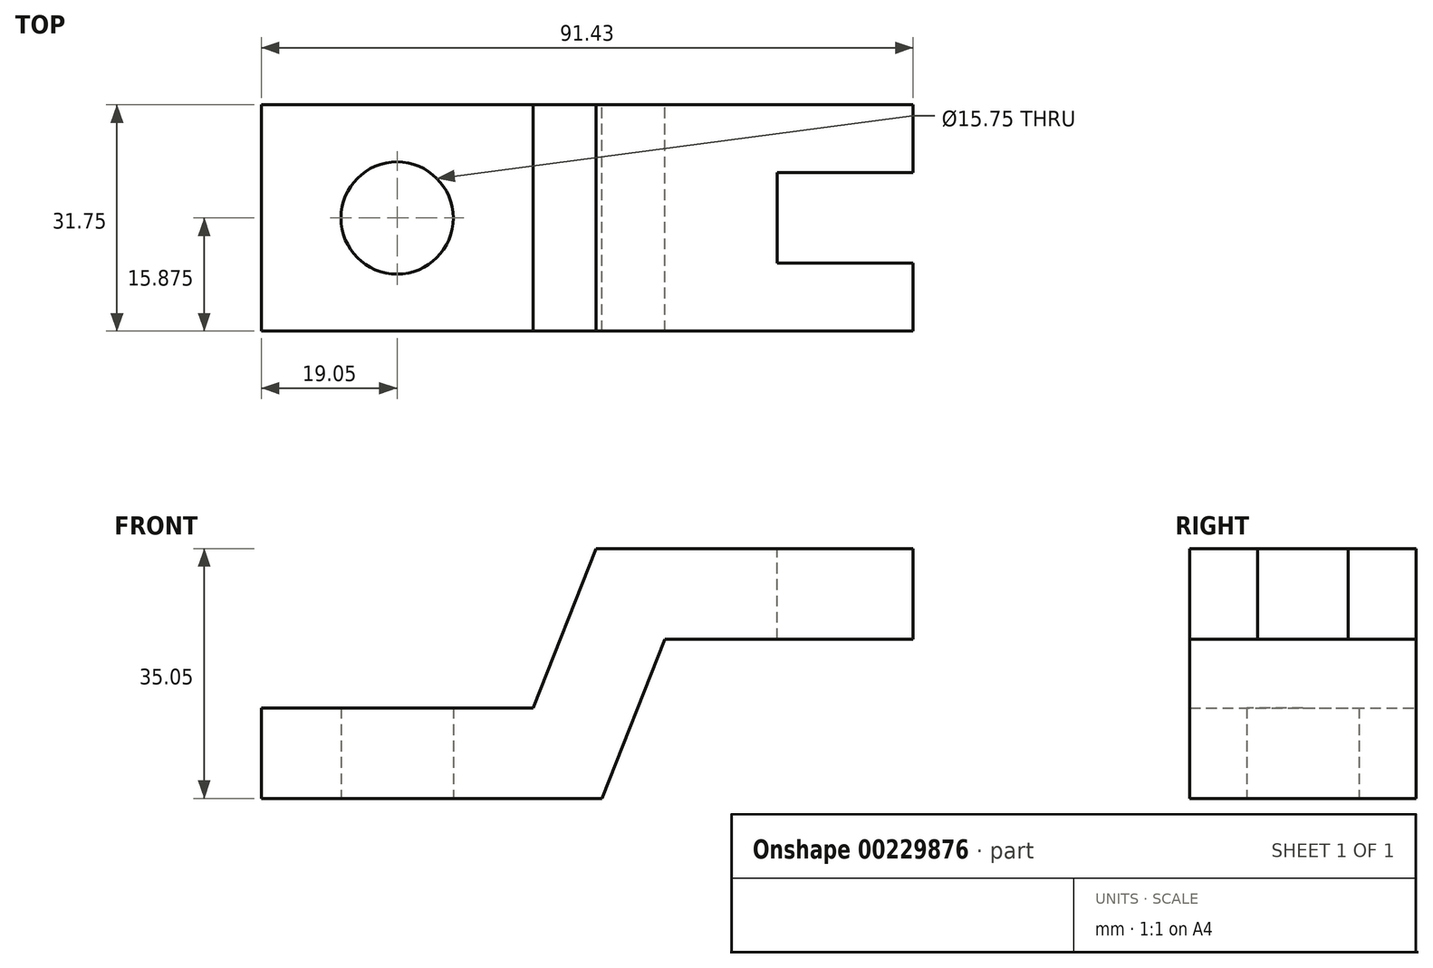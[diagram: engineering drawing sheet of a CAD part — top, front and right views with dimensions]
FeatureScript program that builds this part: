
annotation { "Feature Type Name" : "Feature", "Feature Type Description" : "" }
export const myFeature = defineFeature(function(context is Context, id is Id, definition is map)
    precondition{}
    {
        {
            var Q0;
            Q0=qCreatedBy(makeId("Front.planeOp"),FACE);
            var sketch = newSketch(context, id + "F0", { "sketchPlane" : qUnion([Q0])});
            skLineSegment(sketch, "E0", {"start": v(0, 0) * mm, "end": v(47.75, 0) * mm});
            skLineSegment(sketch, "E1", {"start": v(0, 0) * mm, "end": v(0, 12.7) * mm});
            skLineSegment(sketch, "E2", {"start": v(0, 12.7) * mm, "end": v(38.1, 12.7) * mm});
            skLineSegment(sketch, "E3", {"start": v(91.43, 35.05) * mm, "end": v(91.43, 22.35) * mm});
            skLineSegment(sketch, "E4", {"start": v(91.43, 22.35) * mm, "end": v(56.64, 22.35) * mm});
            skLineSegment(sketch, "E5", {"start": v(91.43, 35.05) * mm, "end": v(46.98, 35.05) * mm});
            skLineSegment(sketch, "E6", {"start": v(56.64, 22.35) * mm, "end": v(47.75, 0) * mm});
            skLineSegment(sketch, "E7", {"start": v(46.98, 35.05) * mm, "end": v(38.1, 12.7) * mm});
            skSolve(sketch);
        }
        {
            var Q0;
            Q0 = qSketchRegion(id + "F0", true);
            extrude(context, id + "F1", {"entities" : qUnion([Q0]), "depth" : 31.75 * mm});
        }
        {
            var Q0;
            Q0=makeQuery(id+"F1.opExtrude","SWEPT_FACE",FACE,{"disambiguationData":[OSD([sQuery(id+"F0.wireOp",EDGE,"E5")])]});
            var sketch = newSketch(context, id + "F2", { "sketchPlane" : qUnion([Q0])});
            skLineSegment(sketch, "E8", {"start": v(91.43, -9.53) * mm, "end": v(72.38, -9.53) * mm});
            skLineSegment(sketch, "E9", {"start": v(91.43, -22.23) * mm, "end": v(72.38, -22.23) * mm});
            skLineSegment(sketch, "E10", {"start": v(72.38, -22.23) * mm, "end": v(72.38, -9.53) * mm});
            skLineSegment(sketch, "E11", {"start": v(91.43, -9.53) * mm, "end": v(91.43, -22.23) * mm});
            skSolve(sketch);
        }
        {
            var Q0;
            Q0 = qSketchRegion(id + "F2", true);
            extrude(context, id + "F3", {"entities" : qUnion([Q0]), "operationType" : NewBodyOperationType.REMOVE, "endBound" : BoundingType.THROUGH_ALL, "oppositeDirection" : true, "depth" : 25.4 * mm});
        }
        {
            var Q0;
            Q0=makeQuery(id+"F1.opExtrude","SWEPT_FACE",FACE,{"disambiguationData":[OSD([sQuery(id+"F0.wireOp",EDGE,"E0")])]});
            var sketch = newSketch(context, id + "F4", { "sketchPlane" : qUnion([Q0])});
            skLineSegment(sketch, "E12", {"start": v(0, 31.75) * mm, "end": v(0, 15.88) * mm});
            skLineSegment(sketch, "E13", {"start": v(0, 15.88) * mm, "end": v(19.05, 15.88) * mm});
            skCircle(sketch, "E14", {"center": v(19.05, 15.88) * mm, "radius": 7.87 * mm});
            skSolve(sketch);
        }
        {
            var Q0;
            Q0 = qSketchRegion(id + "F4", true);
            extrude(context, id + "F5", {"entities" : qUnion([Q0]), "operationType" : NewBodyOperationType.REMOVE, "endBound" : BoundingType.THROUGH_ALL, "oppositeDirection" : true, "depth" : 25.4 * mm});
        }
    });
